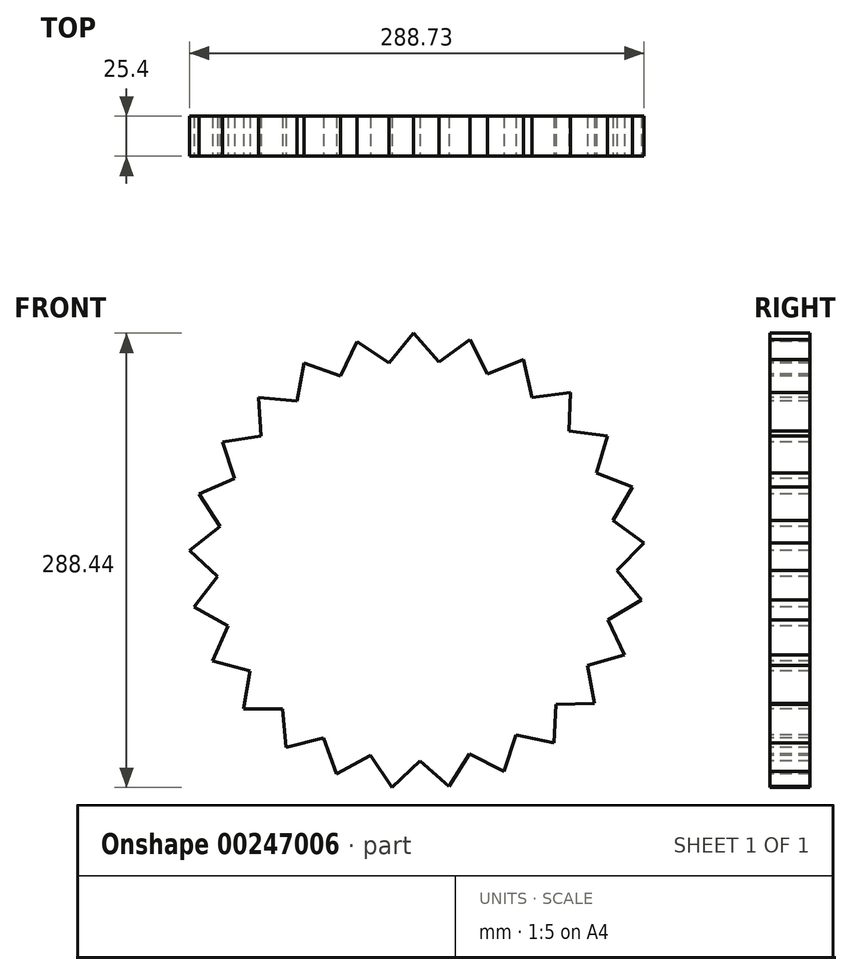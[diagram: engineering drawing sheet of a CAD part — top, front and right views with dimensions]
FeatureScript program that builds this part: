
annotation { "Feature Type Name" : "Feature", "Feature Type Description" : "" }
export const myFeature = defineFeature(function(context is Context, id is Id, definition is map)
    precondition{}
    {
        {
            var Q0;
            Q0=qCreatedBy(makeId("Front.planeOp"),FACE);
            var sketch = newSketch(context, id + "F0", { "sketchPlane" : qUnion([Q0])});
            skCircle(sketch, "E0", {"center": v(0, 0) * mm, "radius": 127 * mm});
            skSolve(sketch);
        }
        {
            var Q0;
            Q0 = qSketchRegion(id + "F0", true);
            extrude(context, id + "F1", {"entities" : qUnion([Q0]), "endBound" : BoundingType.SYMMETRIC, "depth" : 25.4 * mm});
        }
        {
            var Q0;
            Q0=makeQuery(id+"F1.opExtrude","CAP_FACE",FACE,{"disambiguationData":[OSD([sQuery(id+"F0.wireOp",EDGE,"E0")])],"isStart":false});
            var sketch = newSketch(context, id + "F2", { "sketchPlane" : qUnion([Q0])});
            skLineSegment(sketch, "E1", {"start": v(-17.89, 125.73) * mm, "end": v(13.94, 126.23) * mm});
            skLineSegment(sketch, "E2", {"start": v(-17.89, 125.73) * mm, "end": v(-2.26, 144.65) * mm});
            skLineSegment(sketch, "E3", {"start": v(-2.26, 144.65) * mm, "end": v(13.94, 126.23) * mm});
            skLineSegment(sketch, "E4", {"start": v(-17.89, 125.73) * mm, "end": v(0, 0) * mm, "construction": true});
            skLineSegment(sketch, "E5", {"start": v(0, 0) * mm, "end": v(13.94, 126.23) * mm, "construction": true});
            skSolve(sketch);
        }
        {
            var Q0;
            Q0 = qSketchRegion(id + "F2", true);
            extrude(context, id + "F3", {"entities" : qUnion([Q0]), "operationType" : NewBodyOperationType.ADD, "oppositeDirection" : true, "depth" : 25.4 * mm});
        }
        {
            var Q0;
            Q0=makeQuery(id+"F1.opExtrude","SWEPT_BODY",BODY,{"disambiguationData":[OSD([sQuery(id+"F0.wireOp",EDGE,"E0")])]});
            var Q1;
            Q1=makeQuery(id+"F1.opExtrude","SWEPT_FACE",FACE,{"disambiguationData":[OSD([sQuery(id+"F0.wireOp",EDGE,"E0")])]});
            circularPattern(context, id + "F4", {"operationType" : NewBodyOperationType.ADD, "entities" : qUnion([Q0]), "axis" : qUnion([Q1]), "angle" : 360 * degree, "instanceCount" : 25, "equalSpace" : true});
        }
    });
